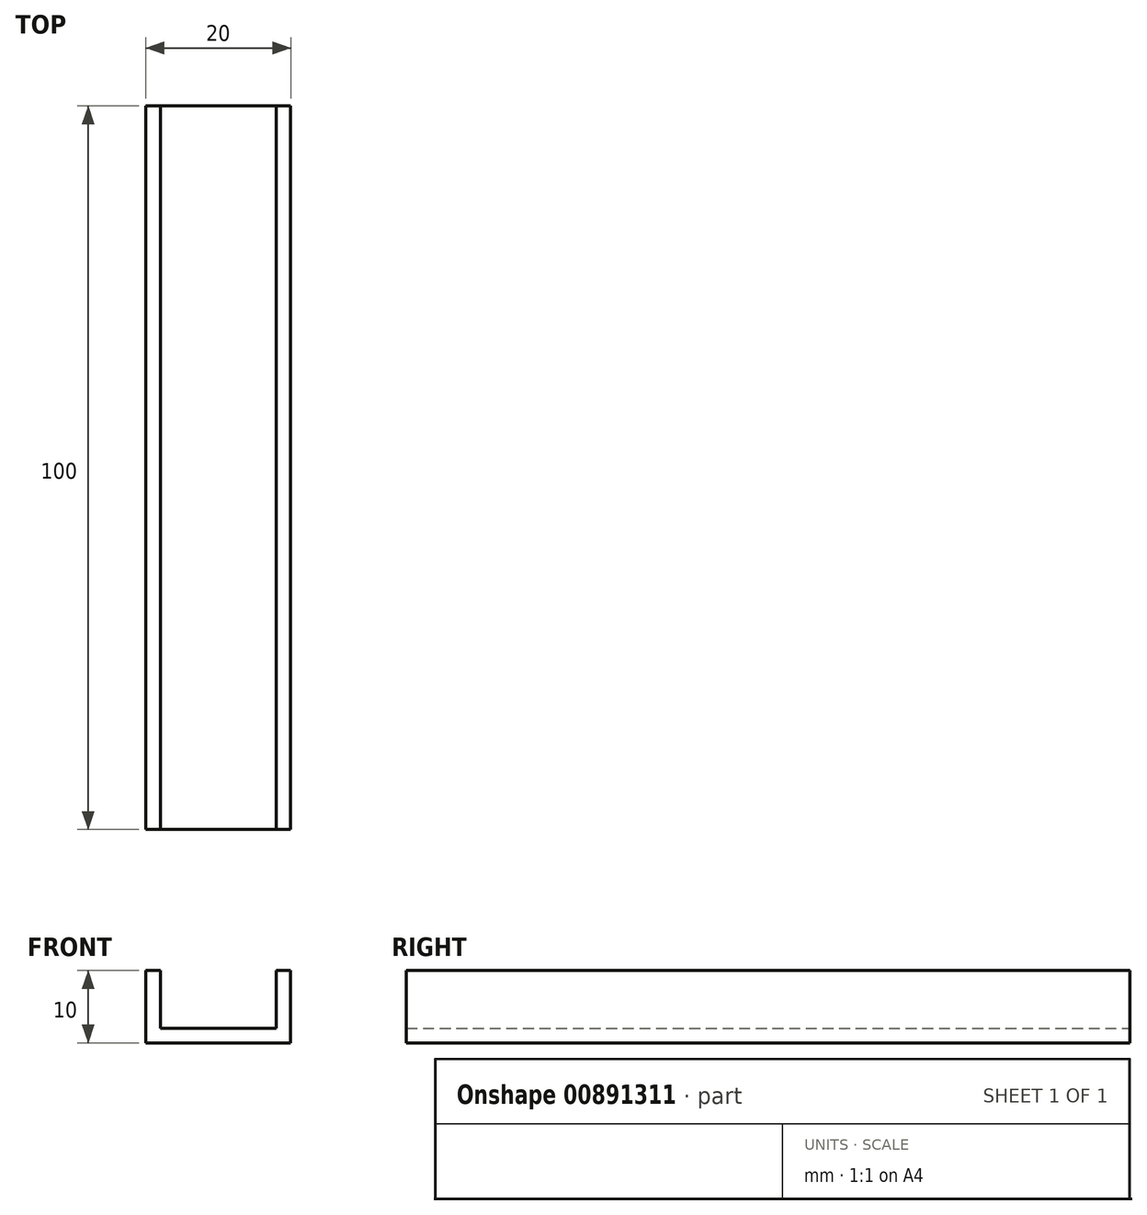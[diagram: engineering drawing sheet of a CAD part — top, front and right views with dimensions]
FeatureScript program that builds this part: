
annotation { "Feature Type Name" : "Feature", "Feature Type Description" : "" }
export const myFeature = defineFeature(function(context is Context, id is Id, definition is map)
    precondition{}
    {
        {
            var Q0;
            Q0=qCreatedBy(makeId("Front.planeOp"),FACE);
            var sketch = newSketch(context, id + "F0", { "sketchPlane" : qUnion([Q0])});
            skLineSegment(sketch, "E0.top", {"start": v(-6.1, -5.3) * mm, "end": v(13.9, -5.3) * mm});
            skLineSegment(sketch, "E0.left", {"start": v(-6.1, 4.7) * mm, "end": v(-6.1, -5.3) * mm});
            skLineSegment(sketch, "E0.right", {"start": v(13.9, 4.7) * mm, "end": v(13.9, -5.3) * mm});
            skPoint(sketch, "E1", {"position": v(13.9, -3.3) * mm});
            skPoint(sketch, "E2", {"position": v(-6.1, -3.3) * mm});
            skLineSegment(sketch, "E3", {"start": v(-4.1, 4.7) * mm, "end": v(-4.1, -5.3) * mm});
            skLineSegment(sketch, "E4", {"start": v(-6.1, -3.3) * mm, "end": v(13.9, -3.3) * mm});
            skLineSegment(sketch, "E5", {"start": v(11.9, 4.7) * mm, "end": v(11.9, -5.3) * mm});
            skPoint(sketch, "E6", {"position": v(-4.1, -3.3) * mm});
            skPoint(sketch, "E7", {"position": v(11.9, -3.3) * mm});
            skPoint(sketch, "E8", {"position": v(-4.1, 4.7) * mm});
            skPoint(sketch, "E9", {"position": v(11.9, 4.7) * mm});
            skPoint(sketch, "E10", {"position": v(13.9, 4.7) * mm});
            skPoint(sketch, "E11", {"position": v(-6.1, 4.7) * mm});
            skPoint(sketch, "E12", {"position": v(-6.1, -5.3) * mm});
            skPoint(sketch, "E13", {"position": v(-4.1, -5.3) * mm});
            skPoint(sketch, "E14", {"position": v(11.9, -5.3) * mm});
            skPoint(sketch, "E15", {"position": v(13.9, -5.3) * mm});
            skLineSegment(sketch, "E16", {"start": v(-6.1, 4.7) * mm, "end": v(-4.1, 4.7) * mm});
            skLineSegment(sketch, "E17", {"start": v(11.9, 4.7) * mm, "end": v(13.9, 4.7) * mm});
            skSolve(sketch);
        }
        {
            var Q0;
            Q0=qSketchRegion(id+"F0",true);
            extrude(context, id + "F1", {"entities" : qUnion([Q0]), "depth" : 100 * mm, "offsetDistance" : 25 * mm});
        }
    });
